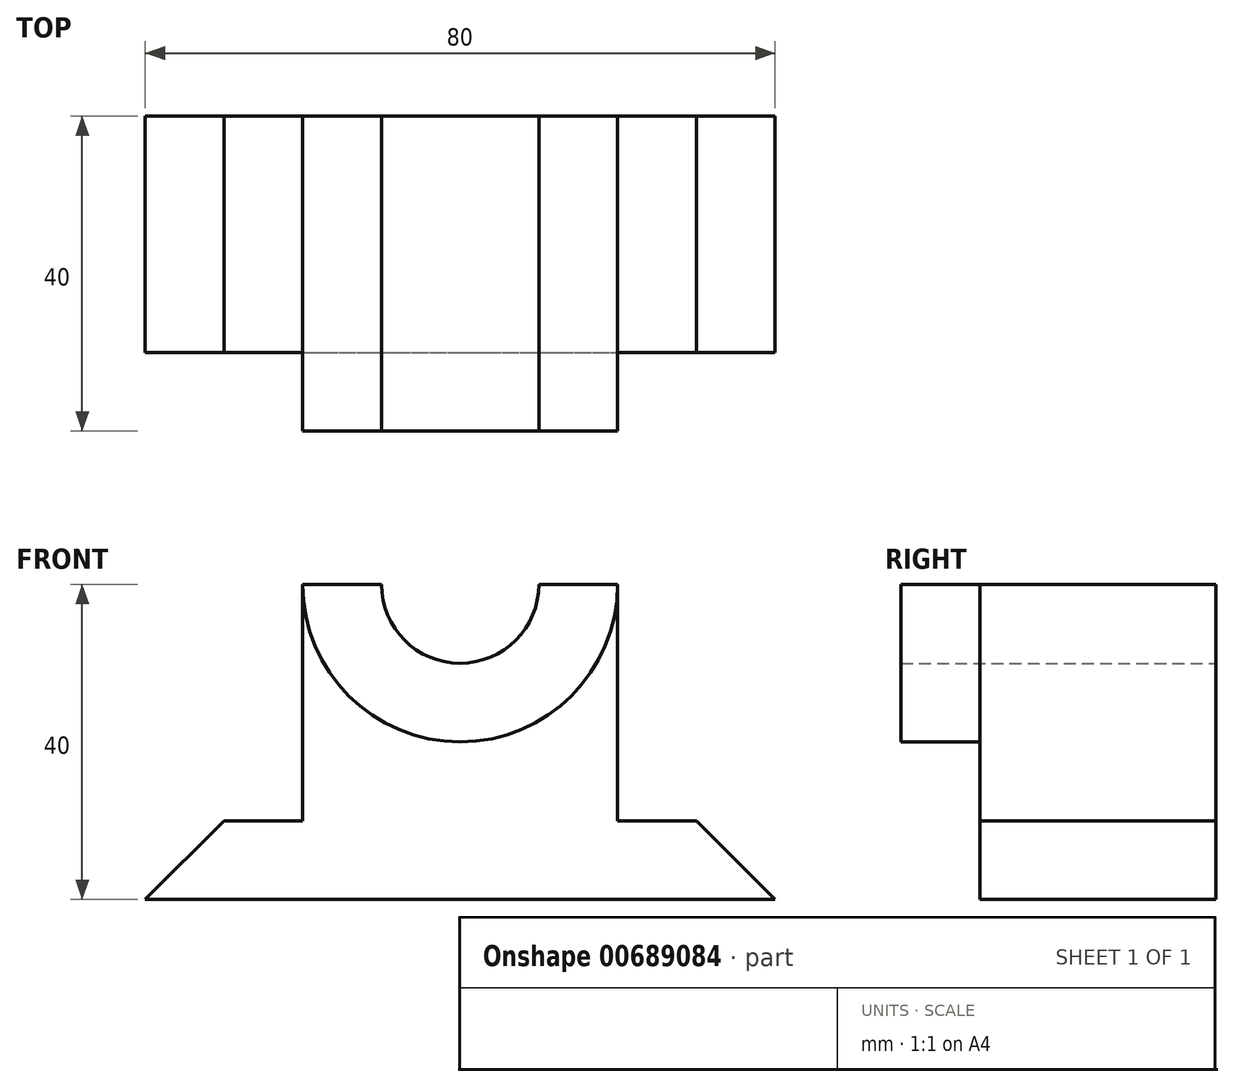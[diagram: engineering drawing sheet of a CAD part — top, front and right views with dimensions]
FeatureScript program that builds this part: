
annotation { "Feature Type Name" : "Feature", "Feature Type Description" : "" }
export const myFeature = defineFeature(function(context is Context, id is Id, definition is map)
    precondition{}
    {
        {
            var Q0;
            Q0=qCreatedBy(makeId("Front.planeOp"),FACE);
            var sketch = newSketch(context, id + "F0", { "sketchPlane" : qUnion([Q0])});
            skLineSegment(sketch, "E0", {"start": v(0, 0) * mm, "end": v(80, 0) * mm});
            skLineSegment(sketch, "E1", {"start": v(80, 0) * mm, "end": v(70, 10) * mm});
            skLineSegment(sketch, "E2", {"start": v(0, 0) * mm, "end": v(10, 10) * mm});
            skLineSegment(sketch, "E3", {"start": v(10, 10) * mm, "end": v(20, 10) * mm});
            skLineSegment(sketch, "E4", {"start": v(70, 10) * mm, "end": v(60, 10) * mm});
            skLineSegment(sketch, "E5", {"start": v(20, 10) * mm, "end": v(20, 40) * mm});
            skLineSegment(sketch, "E6", {"start": v(60, 10) * mm, "end": v(60, 40) * mm});
            skLineSegment(sketch, "E7", {"start": v(20, 40) * mm, "end": v(60, 40) * mm});
            skSolve(sketch);
        }
        {
            var Q0;
            Q0 = qSketchRegion(id + "F0", true);
            extrude(context, id + "F1", {"entities" : qUnion([Q0]), "depth" : 30 * mm, "offsetDistance" : 25 * mm});
        }
        {
            var Q0;
            Q0=makeQuery(id+"F1.opExtrude","CAP_FACE",FACE,{"disambiguationData":[OSD([sQuery(id+"F0.wireOp",EDGE,"E0"),sQuery(id+"F0.wireOp",EDGE,"E1"),sQuery(id+"F0.wireOp",EDGE,"E2"),sQuery(id+"F0.wireOp",EDGE,"E3"),sQuery(id+"F0.wireOp",EDGE,"E4"),sQuery(id+"F0.wireOp",EDGE,"E5"),sQuery(id+"F0.wireOp",EDGE,"E6"),sQuery(id+"F0.wireOp",EDGE,"E7")])],"isStart":false});
            var sketch = newSketch(context, id + "F2", { "sketchPlane" : qUnion([Q0])});
            skLineSegment(sketch, "E8", {"start": v(20, 40) * mm, "end": v(30, 40) * mm});
            skLineSegment(sketch, "E9", {"start": v(60, 40) * mm, "end": v(50, 40) * mm});
            skArc(sketch, "E10", {"start": v(30, 40) * mm, "mid": v(40, 30) * mm, "end": v(50, 40) * mm});
            skArc(sketch, "E11", {"start": v(20, 40) * mm, "mid": v(40, 20) * mm, "end": v(60, 40) * mm});
            skSolve(sketch);
        }
        {
            var Q0;
            Q0=makeQuery(id+"F2.imprint","IMPRINT",FACE,{"disambiguationData":[TD([[makeQuery(id+"F2.imprint","IMPRINT",EDGE,{"derivedFrom":sQuery(id+"F2.wireOp",EDGE,"E8")}),-1.0]])]});
            extrude(context, id + "F3", {"entities" : qUnion([Q0]), "operationType" : NewBodyOperationType.ADD, "depth" : 10 * mm, "offsetDistance" : 25 * mm});
        }
        {
            var Q0;
            {var subQ0=sQuery(id+"F0.wireOp",EDGE,"E7");Q0=makeQuery(id+"F3.boolean.opBoolean","SPLIT",FACE,{"disambiguationData":[TD([makeQuery(id+"F3.opExtrude","SWEPT_FACE",FACE,{"disambiguationData":[OSD([sQuery(id+"F2.wireOp",EDGE,"E10")])]})])],"derivedFrom":makeQuery(id+"F1.opExtrude","CAP_FACE",FACE,{"disambiguationData":[OSD([sQuery(id+"F0.wireOp",EDGE,"E0"),sQuery(id+"F0.wireOp",EDGE,"E1"),sQuery(id+"F0.wireOp",EDGE,"E2"),sQuery(id+"F0.wireOp",EDGE,"E3"),sQuery(id+"F0.wireOp",EDGE,"E4"),sQuery(id+"F0.wireOp",EDGE,"E5"),sQuery(id+"F0.wireOp",EDGE,"E6"),subQ0])],"isStart":false})});}
            extrude(context, id + "F4", {"entities" : qUnion([Q0]), "operationType" : NewBodyOperationType.REMOVE, "oppositeDirection" : true, "depth" : 35 * mm, "offsetDistance" : 25 * mm});
        }
    });
